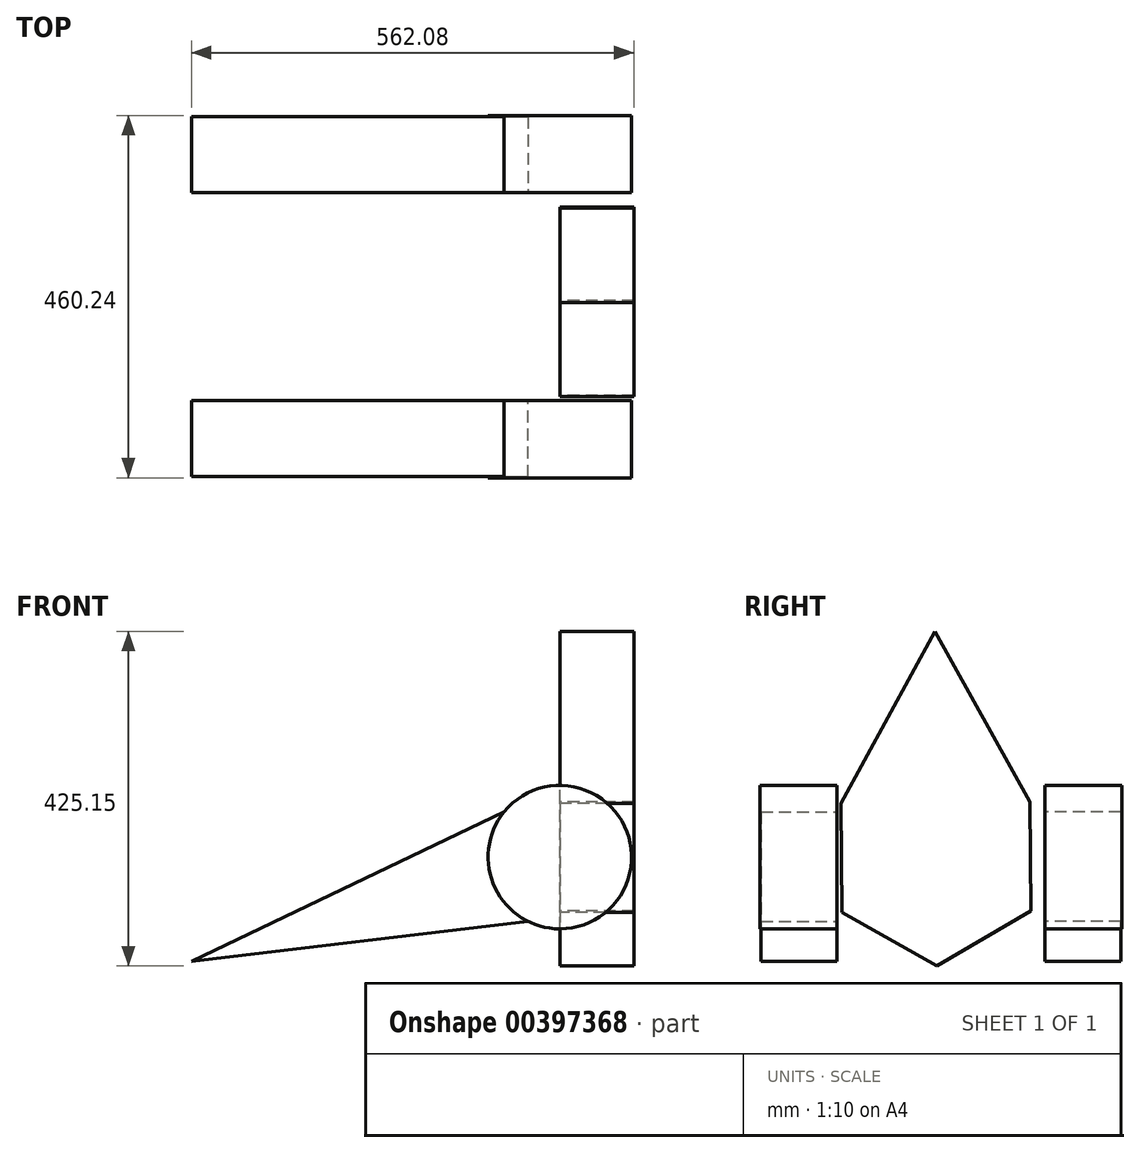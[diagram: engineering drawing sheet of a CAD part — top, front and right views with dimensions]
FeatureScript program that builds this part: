
annotation { "Feature Type Name" : "Feature", "Feature Type Description" : "" }
export const myFeature = defineFeature(function(context is Context, id is Id, definition is map)
    precondition{}
    {
        {
            var Q0;
            Q0=qCreatedBy(makeId("Front.planeOp"),FACE);
            var sketch = newSketch(context, id + "F0", { "sketchPlane" : qUnion([Q0])});
            skCircle(sketch, "E0", {"center": v(0, 0) * mm, "radius": 91.11 * mm});
            skSolve(sketch);
        }
        {
            var Q0;
            Q0=makeQuery(id+"F0.imprint","IMPRINT",FACE,{"disambiguationData":[TD([[makeQuery(id+"F0.imprint","IMPRINT",EDGE,{"derivedFrom":sQuery(id+"F0.wireOp",EDGE,"E0")}),1.0]])]});
            extrude(context, id + "F1", {"entities" : qUnion([Q0]), "depth" : 98.04 * mm});
        }
        {
            var Q0;
            Q0=makeQuery(id+"F1.opExtrude","CAP_FACE",FACE,{"disambiguationData":[OSD([sQuery(id+"F0.wireOp",EDGE,"E0")])],"isStart":true});
            var sketch = newSketch(context, id + "F2", { "sketchPlane" : qUnion([Q0])});
            skLineSegment(sketch, "E1", {"start": v(0, 91.11) * mm, "end": v(-434.23, -92.92) * mm});
            skLineSegment(sketch, "E2", {"start": v(0, -76.65) * mm, "end": v(-434.23, -92.92) * mm});
            skLineSegment(sketch, "E3", {"start": v(0, 91.11) * mm, "end": v(468.1, -132.24) * mm});
            skLineSegment(sketch, "E4", {"start": v(468.1, -132.24) * mm, "end": v(0, -76.65) * mm});
            skSolve(sketch);
        }
        {
            var Q0;
            {var subQ0=sQuery(id+"F2.wireOp",EDGE,"E4");var subQ1=sQuery(id+"F2.wireOp",EDGE,"E3");var subQ2=makeQuery(id+"F2.imprint","INTERSECT",VERTEX,{"derivedFrom":[subQ1,subQ0]});Q0=makeQuery(id+"F2.imprint","IMPRINT",FACE,{"disambiguationData":[TD([[makeQuery(id+"F2.imprint","IMPRINT",EDGE,{"disambiguationData":[TD([[subQ2,1.0]])],"derivedFrom":subQ1}),-1.0]])]});}
            extrude(context, id + "F3", {"entities" : qUnion([Q0]), "operationType" : NewBodyOperationType.ADD, "oppositeDirection" : true, "depth" : 96.52 * mm});
        }
        {
            var Q0;
            Q0=makeQuery(id+"F1.opExtrude","SWEPT_BODY",BODY,{"disambiguationData":[OSD([sQuery(id+"F0.wireOp",EDGE,"E0")])]});
            var Q1;
            Q1=qCreatedBy(makeId("Front.planeOp"),FACE);
            mirror(context, id + "F4", {"entities" : qUnion([Q0]), "mirrorPlane" : qUnion([Q1])});
        }
        {
            var Q0;
            Q0=makeQuery(id+"F4.opPattern","COPY",BODY,{"derivedFrom":makeQuery(id+"F1.opExtrude","SWEPT_BODY",BODY,{"disambiguationData":[OSD([sQuery(id+"F0.wireOp",EDGE,"E0")])]}),"instanceName":"1"});
            transform(context, id + "F5", {"entities" : qUnion([Q0]), "transformType" : TransformType.TRANSLATION_3D, "dx" : 0 * mm, "dy" : 264.16 * mm, "dz" : 0 * mm, "makeCopy" : false});
        }
        {
            var Q0;
            Q0=qCreatedBy(makeId("Right.planeOp"),FACE);
            var sketch = newSketch(context, id + "F6", { "sketchPlane" : qUnion([Q0])});
            skCircle(sketch, "E5.cCircle", {"center": v(125.72, 0) * mm, "radius": 119.75 * mm, "construction": true});
            skLineSegment(sketch, "E5.0", {"start": v(5.37, 68.07) * mm, "end": v(124.5, 138.26) * mm});
            skLineSegment(sketch, "E5.1", {"start": v(124.5, 138.26) * mm, "end": v(244.85, 70.2) * mm});
            skLineSegment(sketch, "E5.2", {"start": v(244.85, 70.2) * mm, "end": v(246.08, -68.07) * mm});
            skLineSegment(sketch, "E5.3", {"start": v(246.08, -68.07) * mm, "end": v(126.95, -138.26) * mm});
            skLineSegment(sketch, "E5.4", {"start": v(126.95, -138.26) * mm, "end": v(6.6, -70.2) * mm});
            skLineSegment(sketch, "E5.5", {"start": v(6.6, -70.2) * mm, "end": v(5.37, 68.07) * mm});
            skPoint(sketch, "E5.0.midPoint", {"position": v(64.93, 103.17) * mm});
            skSolve(sketch);
        }
        {
            var Q0;
            Q0=makeQuery(id+"F6.imprint","IMPRINT",FACE,{"disambiguationData":[TD([[makeQuery(id+"F6.imprint","IMPRINT",EDGE,{"derivedFrom":sQuery(id+"F6.wireOp",EDGE,"E5.0")}),-1.0]])]});
            extrude(context, id + "F7", {"entities" : qUnion([Q0]), "depth" : 93.98 * mm});
        }
        {
            var Q0;
            Q0=makeQuery(id+"F7.opExtrude","CAP_FACE",FACE,{"disambiguationData":[OSD([sQuery(id+"F6.wireOp",EDGE,"E5.0"),sQuery(id+"F6.wireOp",EDGE,"E5.1"),sQuery(id+"F6.wireOp",EDGE,"E5.2"),sQuery(id+"F6.wireOp",EDGE,"E5.3"),sQuery(id+"F6.wireOp",EDGE,"E5.4"),sQuery(id+"F6.wireOp",EDGE,"E5.5")])],"isStart":false});
            var sketch = newSketch(context, id + "F8", { "sketchPlane" : qUnion([Q0])});
            skLineSegment(sketch, "E6", {"start": v(5.37, 68.07) * mm, "end": v(124.5, 286.89) * mm});
            skLineSegment(sketch, "E7", {"start": v(244.85, 70.2) * mm, "end": v(124.5, 286.89) * mm});
            skSolve(sketch);
        }
        {
            var Q0;
            Q0=makeQuery(id+"F8.imprint","IMPRINT",FACE,{"disambiguationData":[TD([[makeQuery(id+"F8.imprint","IMPRINT",EDGE,{"derivedFrom":sQuery(id+"F8.wireOp",EDGE,"E6")}),-1.0]])]});
            extrude(context, id + "F9", {"entities" : qUnion([Q0]), "operationType" : NewBodyOperationType.ADD, "oppositeDirection" : true, "depth" : 93.98 * mm});
        }
    });
